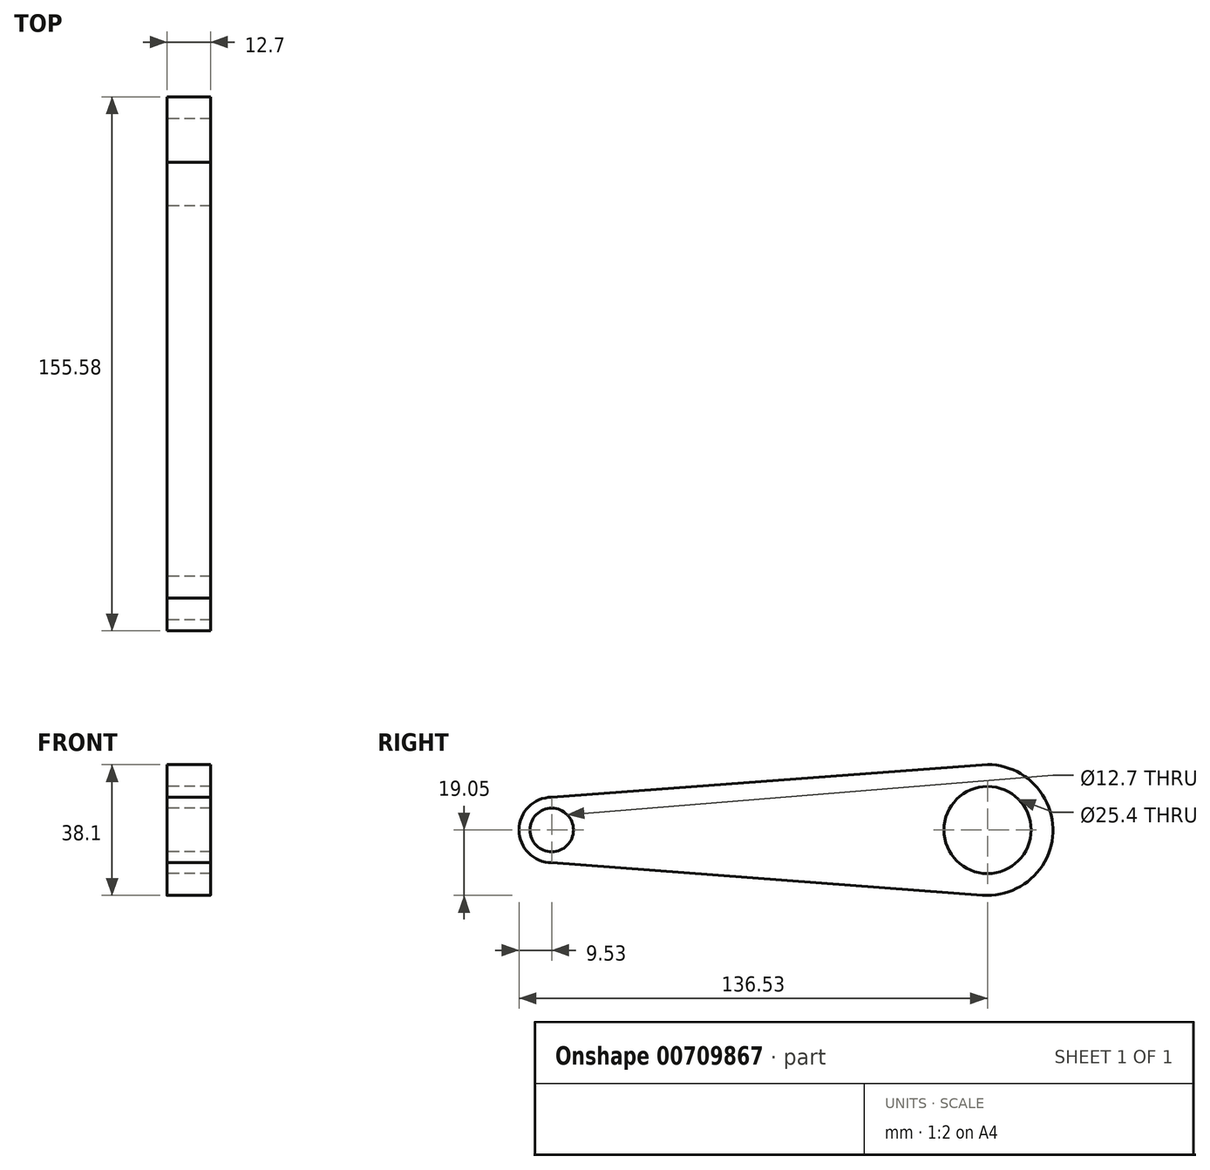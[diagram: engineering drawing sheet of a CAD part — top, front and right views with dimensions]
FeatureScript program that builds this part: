
annotation { "Feature Type Name" : "Feature", "Feature Type Description" : "" }
export const myFeature = defineFeature(function(context is Context, id is Id, definition is map)
    precondition{}
    {
        {
            var Q0;
            Q0=qCreatedBy(makeId("Right.planeOp"),FACE);
            var sketch = newSketch(context, id + "F0", { "sketchPlane" : qUnion([Q0])});
            skLineSegment(sketch, "E0", {"start": v(-76.2, 0) * mm, "end": v(50.8, 0) * mm});
            skCircle(sketch, "E1", {"center": v(50.8, 0) * mm, "radius": 12.7 * mm});
            skCircle(sketch, "E2", {"center": v(-76.2, 0) * mm, "radius": 6.35 * mm});
            skCircle(sketch, "E3", {"center": v(50.8, 0) * mm, "radius": 19.05 * mm});
            skCircle(sketch, "E4", {"center": v(-76.2, 0) * mm, "radius": 9.53 * mm});
            skLineSegment(sketch, "E5", {"start": v(-76.2, 9.52) * mm, "end": v(50.8, 19.05) * mm});
            skLineSegment(sketch, "E6", {"start": v(-76.2, -9.52) * mm, "end": v(50.8, -19.1) * mm});
            skSolve(sketch);
        }
        {
            var Q0;
            Q0=makeQuery(id+"F0.imprint","IMPRINT",FACE,{"disambiguationData":[TD([[makeQuery(id+"F0.imprint","IMPRINT",EDGE,{"derivedFrom":sQuery(id+"F0.wireOp",EDGE,"E2")}),-1.0]])]});
            var Q1;
            {var subQ0=sQuery(id+"F0.wireOp",EDGE,"E3");var subQ1=sQuery(id+"F0.wireOp",EDGE,"E0");var subQ2=makeQuery(id+"F0.imprint","INTERSECT",VERTEX,{"derivedFrom":[subQ1,subQ0]});Q1=makeQuery(id+"F0.imprint","IMPRINT",FACE,{"disambiguationData":[TD([[makeQuery(id+"F0.imprint","IMPRINT",EDGE,{"disambiguationData":[TD([[subQ2,1.0]])],"derivedFrom":subQ1}),1.0]])]});}
            var Q2;
            {var subQ0=sQuery(id+"F0.wireOp",EDGE,"E3");var subQ1=sQuery(id+"F0.wireOp",EDGE,"E0");var subQ2=makeQuery(id+"F0.imprint","INTERSECT",VERTEX,{"derivedFrom":[subQ1,subQ0]});Q2=makeQuery(id+"F0.imprint","IMPRINT",FACE,{"disambiguationData":[TD([[makeQuery(id+"F0.imprint","IMPRINT",EDGE,{"disambiguationData":[TD([[subQ2,1.0]])],"derivedFrom":subQ1}),-1.0]])]});}
            var Q3;
            Q3=makeQuery(id+"F0.imprint","IMPRINT",FACE,{"disambiguationData":[TD([[makeQuery(id+"F0.imprint","IMPRINT",EDGE,{"derivedFrom":sQuery(id+"F0.wireOp",EDGE,"E1")}),-1.0]])]});
            extrude(context, id + "F1", {"entities" : qUnion([Q0, Q1, Q2, Q3]), "endBound" : BoundingType.SYMMETRIC, "depth" : 12.7 * mm, "offsetDistance" : 25.4 * mm});
        }
    });
